# Revit family: Shower_Rail_Caroma Pin
name_source: partatom
category: Plumbing Fixtures
revit_build: Autodesk Revit MEP 2014 (Build: 20140709_2115(x64)
units: mm (PartAtom-declared; Revit-internal decimal feet)

## types (3) — shared parameters
Assembly Code = D2010710
CW Connection = Yes
ConnectorDiameter = 20 mm  [stored 0.0656168 ft]
Default Elevation = 1650 mm
Description = TBC
HW Connection = Yes
Manufacturer = Caroma
ModifiedIssue_ANZRS = 20160203.54 $
Type Comments = Caroma Pin Rail Shower
URL = http://specify.caroma.com.au
Vent Connection = No
WELSRating_ANZRS = WELS 3 star rated, 9L/min
Waste Connection = No
zero-valued in all types: Cost

## per-type parameters (varying)
| type | Material_ANZRS | Model |
| Chrome | Metal-Chrome-Caroma | 87261C3A |
| Black | Metal-Powdercoat-Black-Caroma | 87261B3A |
| White | Metal-Powdercoat-White-Caroma | 87261W3A |

note: [stored X ft] marks values corroborated as IEEE doubles in the binary element streams (Revit-internal decimal feet)

## geometry (parser evidence)
native form markers: Sweep x2
no freeform markers — native parametric forms only
